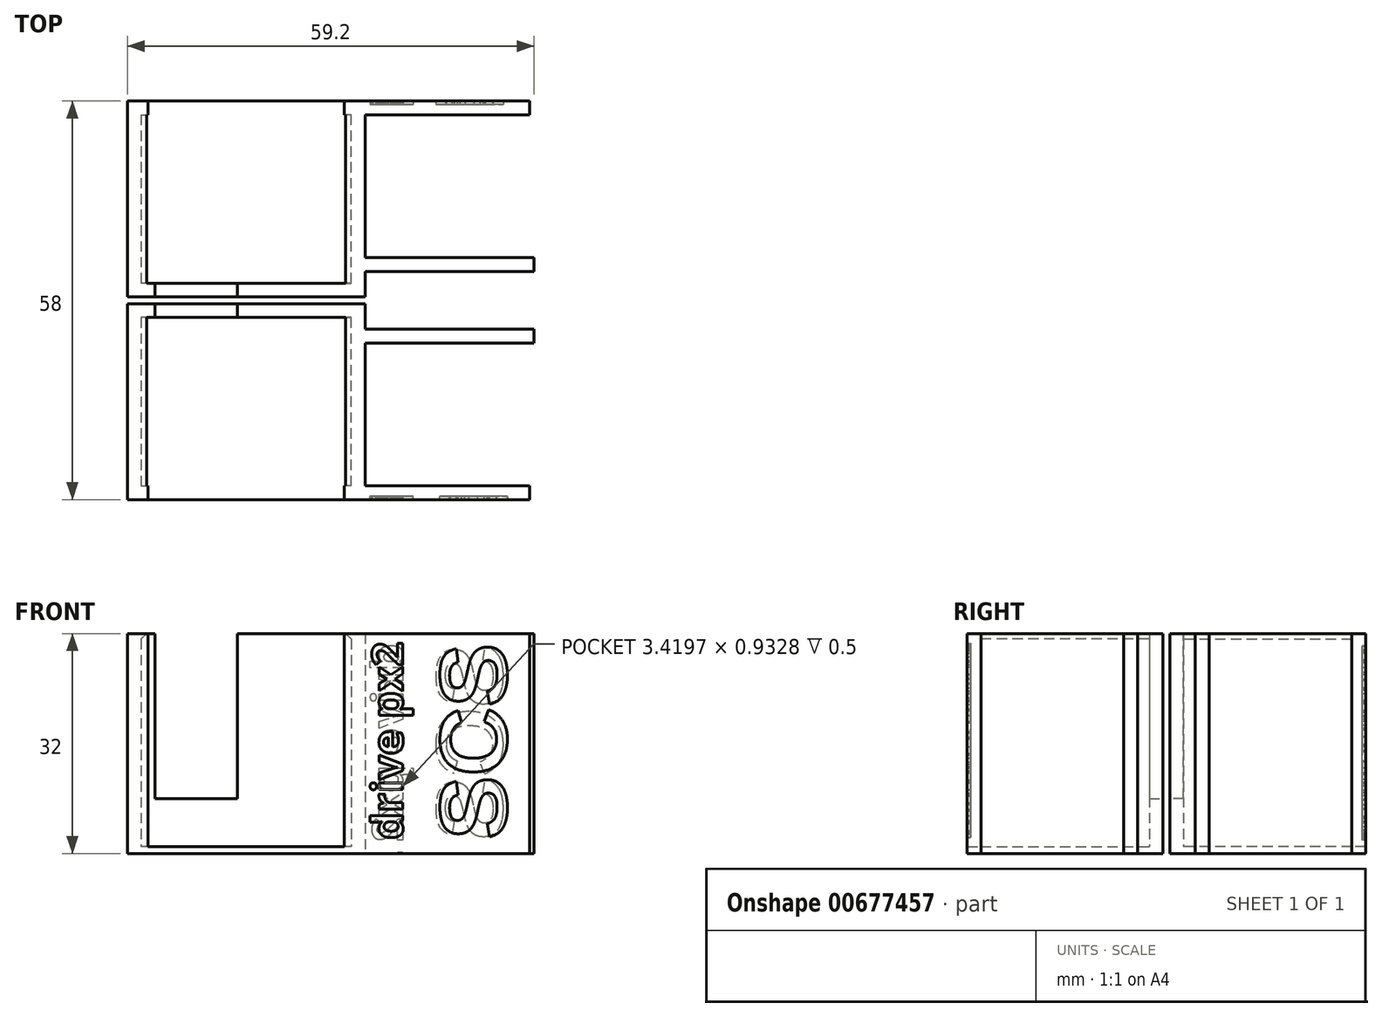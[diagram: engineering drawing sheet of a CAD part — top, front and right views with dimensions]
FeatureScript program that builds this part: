
annotation { "Feature Type Name" : "Feature", "Feature Type Description" : "" }
export const myFeature = defineFeature(function(context is Context, id is Id, definition is map)
    precondition{}
    {
        {
            var Q0;
            Q0=qCreatedBy(makeId("Top.planeOp"),FACE);
            var sketch = newSketch(context, id + "F0", { "sketchPlane" : qUnion([Q0])});
            skLineSegment(sketch, "E0", {"start": v(2, -2) * mm, "end": v(2, 1.7) * mm});
            skLineSegment(sketch, "E1", {"start": v(2, 26.5) * mm, "end": v(0, 26.5) * mm});
            skLineSegment(sketch, "E2", {"start": v(0, 26.5) * mm, "end": v(0, 0) * mm});
            skLineSegment(sketch, "E3", {"start": v(0, 0) * mm, "end": v(-30.6, 0) * mm});
            skLineSegment(sketch, "E4", {"start": v(-30.6, 0) * mm, "end": v(-30.6, 26.5) * mm});
            skLineSegment(sketch, "E5", {"start": v(-30.6, 26.5) * mm, "end": v(-32.6, 26.5) * mm});
            skLineSegment(sketch, "E6", {"start": v(-32.6, 26.5) * mm, "end": v(-32.6, -2) * mm});
            skLineSegment(sketch, "E7", {"start": v(-32.6, -2) * mm, "end": v(2, -2) * mm});
            skLineSegment(sketch, "E8", {"start": v(2, 26.5) * mm, "end": v(2, 26.5) * mm});
            skLineSegment(sketch, "E9", {"start": v(26, 26.5) * mm, "end": v(26, 24.5) * mm});
            skLineSegment(sketch, "E10", {"start": v(26, 24.5) * mm, "end": v(1.4, 24.5) * mm});
            skLineSegment(sketch, "E11.bottom", {"start": v(2, 1.7) * mm, "end": v(26.6, 1.7) * mm});
            skLineSegment(sketch, "E11.top", {"start": v(2, 3.7) * mm, "end": v(26.6, 3.7) * mm});
            skLineSegment(sketch, "E11.left", {"start": v(2, 1.7) * mm, "end": v(2, 3.7) * mm});
            skLineSegment(sketch, "E11.right", {"start": v(26.6, 1.7) * mm, "end": v(26.6, 3.7) * mm});
            skLineSegment(sketch, "E12", {"start": v(2, 1.7) * mm, "end": v(2, 26.5) * mm});
            skLineSegment(sketch, "E13", {"start": v(2, 26.5) * mm, "end": v(26, 26.5) * mm});
            skLineSegment(sketch, "E14.bottom", {"start": v(0, 26.5) * mm, "end": v(-1, 26.5) * mm});
            skLineSegment(sketch, "E14.top", {"start": v(0, 24.5) * mm, "end": v(-1, 24.5) * mm});
            skLineSegment(sketch, "E14.left", {"start": v(0, 26.5) * mm, "end": v(0, 24.5) * mm});
            skLineSegment(sketch, "E14.right", {"start": v(-1, 26.5) * mm, "end": v(-1, 24.5) * mm});
            skLineSegment(sketch, "E15.bottom", {"start": v(-30.6, 26.5) * mm, "end": v(-29.6, 26.5) * mm});
            skLineSegment(sketch, "E15.top", {"start": v(-30.6, 24.5) * mm, "end": v(-29.6, 24.5) * mm});
            skLineSegment(sketch, "E15.left", {"start": v(-30.6, 26.5) * mm, "end": v(-30.6, 24.5) * mm});
            skLineSegment(sketch, "E15.right", {"start": v(-29.6, 26.5) * mm, "end": v(-29.6, 24.5) * mm});
            skSolve(sketch);
        }
        {
            var Q0;
            Q0 = qSketchRegion(id + "F0", true);
            extrude(context, id + "F1", {"entities" : qUnion([Q0]), "depth" : 31 * mm, "offsetDistance" : 25 * mm, "hasSecondDirection" : true, "secondDirectionOppositeDirection" : true, "secondDirectionDepth" : 1 * mm});
        }
        {
            var Q0;
            Q0=qCreatedBy(makeId("Top.planeOp"),FACE);
            var sketch = newSketch(context, id + "F2", { "sketchPlane" : qUnion([Q0])});
            skPoint(sketch, "E16.0", {"position": v(-32.6, 26.5) * mm});
            skPoint(sketch, "E17.0", {"position": v(2, -2) * mm});
            skLineSegment(sketch, "E18.bottom", {"start": v(-32.6, 26.5) * mm, "end": v(2, 26.5) * mm});
            skLineSegment(sketch, "E18.top", {"start": v(-32.6, -2) * mm, "end": v(2, -2) * mm});
            skLineSegment(sketch, "E18.left", {"start": v(-32.6, 26.5) * mm, "end": v(-32.6, -2) * mm});
            skLineSegment(sketch, "E18.right", {"start": v(2, 26.5) * mm, "end": v(2, -2) * mm});
            skSolve(sketch);
        }
        {
            var Q0;
            Q0=makeQuery(id+"F2.imprint","IMPRINT",FACE,{"disambiguationData":[TD([[makeQuery(id+"F2.imprint","IMPRINT",EDGE,{"derivedFrom":sQuery(id+"F2.wireOp",EDGE,"E18.bottom")}),-1.0]])]});
            extrude(context, id + "F3", {"entities" : qUnion([Q0]), "operationType" : NewBodyOperationType.ADD, "oppositeDirection" : true, "depth" : 1 * mm, "offsetDistance" : 25 * mm});
        }
        {
            var Q0;
            Q0=makeQuery(id+"F1.opExtrude","SWEPT_FACE",FACE,{"disambiguationData":[OSD([sQuery(id+"F0.wireOp",EDGE,"E7")])]});
            var sketch = newSketch(context, id + "F4", { "sketchPlane" : qUnion([Q0])});
            skLineSegment(sketch, "E19", {"start": v(-28.6, 31) * mm, "end": v(-28.6, 7) * mm});
            skLineSegment(sketch, "E20", {"start": v(-28.6, 7) * mm, "end": v(-16.6, 7) * mm});
            skLineSegment(sketch, "E21", {"start": v(-16.6, 7) * mm, "end": v(-16.6, 31) * mm});
            skSolve(sketch);
        }
        {
            var Q0;
            {var subQ0=sQuery(id+"F4.wireOp",EDGE,"E19");Q0=makeQuery(id+"F4.imprint","IMPRINT",FACE,{"disambiguationData":[TD([[makeQuery(id+"F4.imprint","IMPRINT",EDGE,{"derivedFrom":subQ0}),1.0]])]});}
            extrude(context, id + "F5", {"entities" : qUnion([Q0]), "operationType" : NewBodyOperationType.REMOVE, "endBound" : BoundingType.UP_TO_NEXT, "oppositeDirection" : true, "depth" : 25 * mm, "offsetDistance" : 25 * mm});
        }
        {
            var Q0;
            Q0=makeQuery(id+"F1.opExtrude","SWEPT_FACE",FACE,{"disambiguationData":[OSD([sQuery(id+"F0.wireOp",EDGE,"E2")])]});
            var sketch = newSketch(context, id + "F6", { "sketchPlane" : qUnion([Q0])});
            skLineSegment(sketch, "E22.0.1", {"start": v(-24.5, 0) * mm, "end": v(0, 0) * mm});
            skLineSegment(sketch, "E22.0.3", {"start": v(0, 31) * mm, "end": v(-24.5, 31) * mm});
            skPoint(sketch, "E23.0", {"position": v(-24.5, 31) * mm});
            skPoint(sketch, "E24.0", {"position": v(0, 31) * mm});
            skLineSegment(sketch, "E25.0", {"start": v(-24.5, 31) * mm, "end": v(0, 31) * mm});
            skLineSegment(sketch, "E26.top", {"start": v(0, 30.2) * mm, "end": v(-24.5, 30.2) * mm});
            skLineSegment(sketch, "E26.left", {"start": v(0, 31) * mm, "end": v(0, 30.2) * mm});
            skLineSegment(sketch, "E26.right", {"start": v(-24.5, 31) * mm, "end": v(-24.5, 30.2) * mm});
            skSolve(sketch);
        }
        {
            var Q0;
            Q0 = qSketchRegion(id + "F6", true);
            extrude(context, id + "F7", {"entities" : qUnion([Q0]), "operationType" : NewBodyOperationType.ADD, "depth" : 1 * mm, "offsetDistance" : 25 * mm});
        }
        {
            var Q0;
            Q0=makeQuery(id+"F7.opExtrude","CAP_EDGE",EDGE,{"disambiguationData":[OSD([sQuery(id+"F6.wireOp",EDGE,"E26.top")])],"isStart":false});
            chamfer(context, id + "F8", {"entities" : qUnion([Q0]), "width" : 1 * mm, "tangentPropagation" : true});
        }
        {
            var Q0;
            Q0=makeQuery(id+"F1.opExtrude","SWEPT_FACE",FACE,{"disambiguationData":[OSD([sQuery(id+"F0.wireOp",EDGE,"E4")])]});
            var sketch = newSketch(context, id + "F9", { "sketchPlane" : qUnion([Q0])});
            skLineSegment(sketch, "E27.0", {"start": v(0, 31) * mm, "end": v(24.5, 31) * mm});
            skLineSegment(sketch, "E28.bottom", {"start": v(24.5, 31) * mm, "end": v(0, 31) * mm});
            skLineSegment(sketch, "E28.top", {"start": v(24.5, 30.2) * mm, "end": v(0, 30.2) * mm});
            skLineSegment(sketch, "E28.left", {"start": v(24.5, 31) * mm, "end": v(24.5, 30.2) * mm});
            skLineSegment(sketch, "E28.right", {"start": v(0, 31) * mm, "end": v(0, 30.2) * mm});
            skSolve(sketch);
        }
        {
            var Q0;
            Q0 = qSketchRegion(id + "F9", true);
            extrude(context, id + "F10", {"entities" : qUnion([Q0]), "operationType" : NewBodyOperationType.ADD, "depth" : 1 * mm, "offsetDistance" : 25 * mm});
        }
        {
            var Q0;
            Q0=makeQuery(id+"F10.opExtrude","CAP_EDGE",EDGE,{"disambiguationData":[OSD([sQuery(id+"F9.wireOp",EDGE,"E28.top")])],"isStart":false});
            chamfer(context, id + "F11", {"entities" : qUnion([Q0]), "width" : 1 * mm, "tangentPropagation" : true});
        }
        {
            var Q0;
            Q0=makeQuery(id+"F1.opExtrude","SWEPT_BODY",BODY,{"disambiguationData":[OSD([sQuery(id+"F0.wireOp",EDGE,"E0"),sQuery(id+"F0.wireOp",EDGE,"E1"),sQuery(id+"F0.wireOp",EDGE,"E2"),sQuery(id+"F0.wireOp",EDGE,"E3"),sQuery(id+"F0.wireOp",EDGE,"E4"),sQuery(id+"F0.wireOp",EDGE,"E5"),sQuery(id+"F0.wireOp",EDGE,"E6"),sQuery(id+"F0.wireOp",EDGE,"E7"),sQuery(id+"F0.wireOp",EDGE,"E9"),sQuery(id+"F0.wireOp",EDGE,"E10"),sQuery(id+"F0.wireOp",EDGE,"E11.bottom"),sQuery(id+"F0.wireOp",EDGE,"E11.top"),sQuery(id+"F0.wireOp",EDGE,"E11.right"),sQuery(id+"F0.wireOp",EDGE,"E12"),sQuery(id+"F0.wireOp",EDGE,"E13"),sQuery(id+"F0.wireOp",EDGE,"E14.bottom"),sQuery(id+"F0.wireOp",EDGE,"E14.top"),sQuery(id+"F0.wireOp",EDGE,"E14.right"),sQuery(id+"F0.wireOp",EDGE,"E15.bottom"),sQuery(id+"F0.wireOp",EDGE,"E15.top"),sQuery(id+"F0.wireOp",EDGE,"E15.right")])]});
            var Q1;
            Q1=qCreatedBy(makeId("Top.planeOp"),FACE);
            mirror(context, id + "F12", {"entities" : qUnion([Q0]), "mirrorPlane" : qUnion([Q1])});
        }
        {
            var Q0;
            Q0=makeQuery(id+"F1.opExtrude","SWEPT_FACE",FACE,{"disambiguationData":[OSD([sQuery(id+"F0.wireOp",EDGE,"E13")])]});
            var sketch = newSketch(context, id + "F13", { "sketchPlane" : qUnion([Q0])});
            skText(sketch, "E29", { "text": "SCS", "fontName": "Arimo-Bold.ttf"});
            skLineSegment(sketch, "E30", {"start": v(-22, 31) * mm, "end": v(-22, -1) * mm});
            skText(sketch, "E31", { "text": "drive px2", "fontName": "OpenSans-Bold.ttf"});
            const initialGuessF13  = {"E29": [-0.022, 0.0295, 0, -1, 0.01], "E31": [-0.00751, 0.0295, 0, -1, 0.00451]};
            skSetInitialGuess(sketch, initialGuessF13);
            skSolve(sketch);
        }
        {
            var Q0;
            Q0=makeQuery(id+"F12.opPattern","COPY",FACE,{"derivedFrom":makeQuery(id+"F3.boolean.opBoolean","MERGE",FACE,{"derivedFrom":[makeQuery(id+"F1.opExtrude","SWEPT_FACE",FACE,{"disambiguationData":[OSD([sQuery(id+"F0.wireOp",EDGE,"E1"),sQuery(id+"F0.wireOp",EDGE,"E13"),sQuery(id+"F0.wireOp",EDGE,"E14.bottom")])]}),makeQuery(id+"F1.opExtrude","SWEPT_FACE",FACE,{"disambiguationData":[OSD([sQuery(id+"F0.wireOp",EDGE,"E5"),sQuery(id+"F0.wireOp",EDGE,"E15.bottom")])]}),makeQuery(id+"F3.opExtrude","SWEPT_FACE",FACE,{"disambiguationData":[OSD([sQuery(id+"F2.wireOp",EDGE,"E18.bottom")])]})]}),"instanceName":"1"});
            var sketch = newSketch(context, id + "F14", { "sketchPlane" : qUnion([Q0])});
            skText(sketch, "E32", { "text": "SCS", "fontName": "Arimo-Bold.ttf"});
            skLineSegment(sketch, "E33", {"start": v(-22.6, 0.5) * mm, "end": v(-22.6, -31.5) * mm});
            skText(sketch, "E34", { "text": "drive px2", "fontName": "OpenSans-Bold.ttf"});
            const initialGuessF14  = {"E32": [-0.0226, -0.00102, 0, -1, 0.01], "E34": [-0.00751, -0.00102, 0, -1, 0.00451]};
            skSetInitialGuess(sketch, initialGuessF14);
            skSolve(sketch);
        }
        {
            var Q0;
            Q0=makeQuery(id+"F13.imprint","IMPRINT",FACE,{"disambiguationData":[TD([[makeQuery(id+"F13.imprint","IMPRINT",EDGE,{"derivedFrom":sQuery(id+"F13.wireOp",EDGE,"E31.sketch_text.stroke-75")}),-1.0]])]});
            var Q1;
            Q1=makeQuery(id+"F13.imprint","IMPRINT",FACE,{"disambiguationData":[TD([[makeQuery(id+"F13.imprint","IMPRINT",EDGE,{"derivedFrom":sQuery(id+"F13.wireOp",EDGE,"E31.sketch_text.stroke-110")}),-1.0]])]});
            var Q2;
            Q2=makeQuery(id+"F13.imprint","IMPRINT",FACE,{"disambiguationData":[TD([[makeQuery(id+"F13.imprint","IMPRINT",EDGE,{"derivedFrom":sQuery(id+"F13.wireOp",EDGE,"E31.sketch_text.stroke-36")}),-1.0]])]});
            var Q3;
            Q3=makeQuery(id+"F13.imprint","IMPRINT",FACE,{"disambiguationData":[TD([[makeQuery(id+"F13.imprint","IMPRINT",EDGE,{"derivedFrom":sQuery(id+"F13.wireOp",EDGE,"E31.sketch_text.stroke-98")}),-1.0]])]});
            var Q4;
            Q4=makeQuery(id+"F13.imprint","IMPRINT",FACE,{"disambiguationData":[TD([[makeQuery(id+"F13.imprint","IMPRINT",EDGE,{"derivedFrom":sQuery(id+"F13.wireOp",EDGE,"E29.sketch_text.stroke-31")}),-1.0]])]});
            var Q5;
            Q5=makeQuery(id+"F13.imprint","IMPRINT",FACE,{"disambiguationData":[TD([[makeQuery(id+"F13.imprint","IMPRINT",EDGE,{"derivedFrom":sQuery(id+"F13.wireOp",EDGE,"E31.sketch_text.stroke-55")}),-1.0]])]});
            var Q6;
            {var subQ0=sQuery(id+"F13.wireOp",EDGE,"E29.sketch_text.stroke-2");var subQ1=sQuery(id+"F13.wireOp",EDGE,"E29.sketch_text.stroke-1");var subQ2=makeQuery(id+"F13.imprint","INTERSECT",VERTEX,{"derivedFrom":[subQ1,subQ0]});Q6=makeQuery(id+"F13.imprint","IMPRINT",FACE,{"disambiguationData":[TD([[makeQuery(id+"F13.imprint","IMPRINT",EDGE,{"disambiguationData":[TD([[subQ2,1.0]])],"derivedFrom":subQ1}),-1.0]])]});}
            var Q7;
            Q7=makeQuery(id+"F13.imprint","IMPRINT",FACE,{"disambiguationData":[TD([[makeQuery(id+"F13.imprint","IMPRINT",EDGE,{"derivedFrom":sQuery(id+"F13.wireOp",EDGE,"E31.sketch_text.stroke-0")}),-1.0]])]});
            var Q8;
            {var subQ5=sQuery(id+"F13.wireOp",EDGE,"E29.sketch_text.stroke-48");Q8=makeQuery(id+"F13.imprint","IMPRINT",FACE,{"disambiguationData":[TD([[makeQuery(id+"F13.imprint","IMPRINT",EDGE,{"derivedFrom":subQ5}),-1.0]])]});}
            var Q9;
            {var subQ5=sQuery(id+"F13.wireOp",EDGE,"E29.sketch_text.stroke-0");Q9=makeQuery(id+"F13.imprint","IMPRINT",FACE,{"disambiguationData":[TD([[makeQuery(id+"F13.imprint","IMPRINT",EDGE,{"derivedFrom":subQ5}),-1.0]])]});}
            var Q10;
            Q10=makeQuery(id+"F13.imprint","IMPRINT",FACE,{"disambiguationData":[TD([[makeQuery(id+"F13.imprint","IMPRINT",EDGE,{"derivedFrom":sQuery(id+"F13.wireOp",EDGE,"E31.sketch_text.stroke-41")}),-1.0]])]});
            var Q11;
            Q11=makeQuery(id+"F13.imprint","IMPRINT",FACE,{"disambiguationData":[TD([[makeQuery(id+"F13.imprint","IMPRINT",EDGE,{"derivedFrom":sQuery(id+"F13.wireOp",EDGE,"E31.sketch_text.stroke-23")}),-1.0]])]});
            var Q12;
            Q12=makeQuery(id+"F13.imprint","IMPRINT",FACE,{"disambiguationData":[TD([[makeQuery(id+"F13.imprint","IMPRINT",EDGE,{"derivedFrom":sQuery(id+"F13.wireOp",EDGE,"E31.sketch_text.stroke-45")}),-1.0]])]});
            var Q13;
            {var subQ0=sQuery(id+"F13.wireOp",EDGE,"E29.sketch_text.stroke-50");var subQ1=sQuery(id+"F13.wireOp",EDGE,"E29.sketch_text.stroke-49");var subQ2=makeQuery(id+"F13.imprint","INTERSECT",VERTEX,{"derivedFrom":[subQ1,subQ0]});Q13=makeQuery(id+"F13.imprint","IMPRINT",FACE,{"disambiguationData":[TD([[makeQuery(id+"F13.imprint","IMPRINT",EDGE,{"disambiguationData":[TD([[subQ2,1.0]])],"derivedFrom":subQ1}),-1.0]])]});}
            var Q14;
            {var subQ0=sQuery(id+"F13.wireOp",EDGE,"E29.sketch_text.stroke-35");var subQ1=sQuery(id+"F13.wireOp",EDGE,"E29.sketch_text.stroke-34");var subQ2=makeQuery(id+"F13.imprint","INTERSECT",VERTEX,{"derivedFrom":[subQ1,subQ0]});Q14=makeQuery(id+"F13.imprint","IMPRINT",FACE,{"disambiguationData":[TD([[makeQuery(id+"F13.imprint","IMPRINT",EDGE,{"disambiguationData":[TD([[subQ2,1.0]])],"derivedFrom":subQ1}),-1.0]])]});}
            var Q15;
            Q15=makeQuery(id+"F14.imprint","IMPRINT",FACE,{"disambiguationData":[TD([[makeQuery(id+"F14.imprint","IMPRINT",EDGE,{"derivedFrom":sQuery(id+"F14.wireOp",EDGE,"E34.sketch_text.stroke-0")}),-1.0]])]});
            var Q16;
            Q16=makeQuery(id+"F14.imprint","IMPRINT",FACE,{"disambiguationData":[TD([[makeQuery(id+"F14.imprint","IMPRINT",EDGE,{"derivedFrom":sQuery(id+"F14.wireOp",EDGE,"E34.sketch_text.stroke-23")}),-1.0]])]});
            var Q17;
            Q17=makeQuery(id+"F14.imprint","IMPRINT",FACE,{"disambiguationData":[TD([[makeQuery(id+"F14.imprint","IMPRINT",EDGE,{"derivedFrom":sQuery(id+"F14.wireOp",EDGE,"E34.sketch_text.stroke-41")}),-1.0]])]});
            var Q18;
            Q18=makeQuery(id+"F14.imprint","IMPRINT",FACE,{"disambiguationData":[TD([[makeQuery(id+"F14.imprint","IMPRINT",EDGE,{"derivedFrom":sQuery(id+"F14.wireOp",EDGE,"E34.sketch_text.stroke-45")}),-1.0]])]});
            var Q19;
            Q19=makeQuery(id+"F14.imprint","IMPRINT",FACE,{"disambiguationData":[TD([[makeQuery(id+"F14.imprint","IMPRINT",EDGE,{"derivedFrom":sQuery(id+"F14.wireOp",EDGE,"E34.sketch_text.stroke-55")}),-1.0]])]});
            var Q20;
            Q20=makeQuery(id+"F14.imprint","IMPRINT",FACE,{"disambiguationData":[TD([[makeQuery(id+"F14.imprint","IMPRINT",EDGE,{"derivedFrom":sQuery(id+"F14.wireOp",EDGE,"E34.sketch_text.stroke-36")}),-1.0]])]});
            var Q21;
            Q21=makeQuery(id+"F14.imprint","IMPRINT",FACE,{"disambiguationData":[TD([[makeQuery(id+"F14.imprint","IMPRINT",EDGE,{"derivedFrom":sQuery(id+"F14.wireOp",EDGE,"E34.sketch_text.stroke-75")}),-1.0]])]});
            var Q22;
            Q22=makeQuery(id+"F14.imprint","IMPRINT",FACE,{"disambiguationData":[TD([[makeQuery(id+"F14.imprint","IMPRINT",EDGE,{"derivedFrom":sQuery(id+"F14.wireOp",EDGE,"E34.sketch_text.stroke-98")}),-1.0]])]});
            var Q23;
            Q23=makeQuery(id+"F14.imprint","IMPRINT",FACE,{"disambiguationData":[TD([[makeQuery(id+"F14.imprint","IMPRINT",EDGE,{"derivedFrom":sQuery(id+"F14.wireOp",EDGE,"E34.sketch_text.stroke-110")}),-1.0]])]});
            var Q24;
            {var subQ5=sQuery(id+"F14.wireOp",EDGE,"E32.sketch_text.stroke-48");Q24=makeQuery(id+"F14.imprint","IMPRINT",FACE,{"disambiguationData":[TD([[makeQuery(id+"F14.imprint","IMPRINT",EDGE,{"derivedFrom":subQ5}),-1.0]])]});}
            var Q25;
            Q25=makeQuery(id+"F14.imprint","IMPRINT",FACE,{"disambiguationData":[TD([[makeQuery(id+"F14.imprint","IMPRINT",EDGE,{"derivedFrom":sQuery(id+"F14.wireOp",EDGE,"E32.sketch_text.stroke-31")}),-1.0]])]});
            var Q26;
            {var subQ5=sQuery(id+"F14.wireOp",EDGE,"E32.sketch_text.stroke-0");Q26=makeQuery(id+"F14.imprint","IMPRINT",FACE,{"disambiguationData":[TD([[makeQuery(id+"F14.imprint","IMPRINT",EDGE,{"derivedFrom":subQ5}),-1.0]])]});}
            extrude(context, id + "F15", {"entities" : qUnion([Q0, Q1, Q2, Q3, Q4, Q5, Q6, Q7, Q8, Q9, Q10, Q11, Q12, Q13, Q14, Q15, Q16, Q17, Q18, Q19, Q20, Q21, Q22, Q23, Q24, Q25, Q26]), "operationType" : NewBodyOperationType.REMOVE, "endBound" : BoundingType.SYMMETRIC, "depth" : 1 * mm, "offsetDistance" : 25 * mm});
        }
        {
            var Q0;
            Q0 = qSketchRegion(id + "F14", true);
            extrude(context, id + "F16", {"entities" : qUnion([Q0]), "operationType" : NewBodyOperationType.REMOVE, "surfaceOperationType" : NewSurfaceOperationType.ADD, "endBound" : BoundingType.SYMMETRIC, "oppositeDirection" : true, "depth" : 1 * mm, "offsetDistance" : 25 * mm});
        }
        {
            var Q0;
            Q0=makeQuery(id+"F12.opPattern","COPY",BODY,{"derivedFrom":makeQuery(id+"F1.opExtrude","SWEPT_BODY",BODY,{"disambiguationData":[OSD([sQuery(id+"F0.wireOp",EDGE,"E0"),sQuery(id+"F0.wireOp",EDGE,"E1"),sQuery(id+"F0.wireOp",EDGE,"E2"),sQuery(id+"F0.wireOp",EDGE,"E3"),sQuery(id+"F0.wireOp",EDGE,"E4"),sQuery(id+"F0.wireOp",EDGE,"E5"),sQuery(id+"F0.wireOp",EDGE,"E6"),sQuery(id+"F0.wireOp",EDGE,"E7"),sQuery(id+"F0.wireOp",EDGE,"E9"),sQuery(id+"F0.wireOp",EDGE,"E10"),sQuery(id+"F0.wireOp",EDGE,"E11.bottom"),sQuery(id+"F0.wireOp",EDGE,"E11.top"),sQuery(id+"F0.wireOp",EDGE,"E11.right"),sQuery(id+"F0.wireOp",EDGE,"E12"),sQuery(id+"F0.wireOp",EDGE,"E13"),sQuery(id+"F0.wireOp",EDGE,"E14.bottom"),sQuery(id+"F0.wireOp",EDGE,"E14.top"),sQuery(id+"F0.wireOp",EDGE,"E14.right"),sQuery(id+"F0.wireOp",EDGE,"E15.bottom"),sQuery(id+"F0.wireOp",EDGE,"E15.top"),sQuery(id+"F0.wireOp",EDGE,"E15.right")])]}),"instanceName":"1"});
            transform(context, id + "F17", {"entities" : qUnion([Q0]), "transformType" : TransformType.TRANSLATION_3D, "dx" : 0 * mm, "dy" : 0 * mm, "dz" : -2 * mm, "makeCopy" : false});
        }
        {
            var Q0;
            Q0=makeQuery(id+"F12.opPattern","COPY",BODY,{"derivedFrom":makeQuery(id+"F1.opExtrude","SWEPT_BODY",BODY,{"disambiguationData":[OSD([sQuery(id+"F0.wireOp",EDGE,"E0"),sQuery(id+"F0.wireOp",EDGE,"E1"),sQuery(id+"F0.wireOp",EDGE,"E2"),sQuery(id+"F0.wireOp",EDGE,"E3"),sQuery(id+"F0.wireOp",EDGE,"E4"),sQuery(id+"F0.wireOp",EDGE,"E5"),sQuery(id+"F0.wireOp",EDGE,"E6"),sQuery(id+"F0.wireOp",EDGE,"E7"),sQuery(id+"F0.wireOp",EDGE,"E9"),sQuery(id+"F0.wireOp",EDGE,"E10"),sQuery(id+"F0.wireOp",EDGE,"E11.bottom"),sQuery(id+"F0.wireOp",EDGE,"E11.top"),sQuery(id+"F0.wireOp",EDGE,"E11.right"),sQuery(id+"F0.wireOp",EDGE,"E12"),sQuery(id+"F0.wireOp",EDGE,"E13"),sQuery(id+"F0.wireOp",EDGE,"E14.bottom"),sQuery(id+"F0.wireOp",EDGE,"E14.top"),sQuery(id+"F0.wireOp",EDGE,"E14.right"),sQuery(id+"F0.wireOp",EDGE,"E15.bottom"),sQuery(id+"F0.wireOp",EDGE,"E15.top"),sQuery(id+"F0.wireOp",EDGE,"E15.right")])]}),"instanceName":"1"});
            var Q1;
            Q1=makeQuery(id+"F3.boolean.opBoolean","MERGE",EDGE,{"derivedFrom":[makeQuery(id+"F1.opExtrude","CAP_EDGE",EDGE,{"disambiguationData":[OSD([sQuery(id+"F0.wireOp",EDGE,"E1"),sQuery(id+"F0.wireOp",EDGE,"E13"),sQuery(id+"F0.wireOp",EDGE,"E14.bottom")])],"isStart":true}),makeQuery(id+"F1.opExtrude","CAP_EDGE",EDGE,{"disambiguationData":[OSD([sQuery(id+"F0.wireOp",EDGE,"E5"),sQuery(id+"F0.wireOp",EDGE,"E15.bottom")])],"isStart":true}),makeQuery(id+"F3.opExtrude","CAP_EDGE",EDGE,{"disambiguationData":[OSD([sQuery(id+"F2.wireOp",EDGE,"E18.bottom")])],"isStart":false})]});
            transform(context, id + "F18", {"entities" : qUnion([Q0]), "transformType" : TransformType.ROTATION, "transformAxis" : qUnion([Q1]), "angle" : 180 * degree, "makeCopy" : false});
        }
        {
            var Q0;
            Q0=makeQuery(id+"F12.opPattern","COPY",BODY,{"derivedFrom":makeQuery(id+"F1.opExtrude","SWEPT_BODY",BODY,{"disambiguationData":[OSD([sQuery(id+"F0.wireOp",EDGE,"E0"),sQuery(id+"F0.wireOp",EDGE,"E1"),sQuery(id+"F0.wireOp",EDGE,"E2"),sQuery(id+"F0.wireOp",EDGE,"E3"),sQuery(id+"F0.wireOp",EDGE,"E4"),sQuery(id+"F0.wireOp",EDGE,"E5"),sQuery(id+"F0.wireOp",EDGE,"E6"),sQuery(id+"F0.wireOp",EDGE,"E7"),sQuery(id+"F0.wireOp",EDGE,"E9"),sQuery(id+"F0.wireOp",EDGE,"E10"),sQuery(id+"F0.wireOp",EDGE,"E11.bottom"),sQuery(id+"F0.wireOp",EDGE,"E11.top"),sQuery(id+"F0.wireOp",EDGE,"E11.right"),sQuery(id+"F0.wireOp",EDGE,"E12"),sQuery(id+"F0.wireOp",EDGE,"E13"),sQuery(id+"F0.wireOp",EDGE,"E14.bottom"),sQuery(id+"F0.wireOp",EDGE,"E14.top"),sQuery(id+"F0.wireOp",EDGE,"E14.right"),sQuery(id+"F0.wireOp",EDGE,"E15.bottom"),sQuery(id+"F0.wireOp",EDGE,"E15.top"),sQuery(id+"F0.wireOp",EDGE,"E15.right")])]}),"instanceName":"1"});
            transform(context, id + "F19", {"entities" : qUnion([Q0]), "transformType" : TransformType.TRANSLATION_3D, "dx" : 0 * mm, "dy" : -58 * mm, "dz" : 0 * mm, "makeCopy" : false});
        }
    });
